# Revit family: FU_Chair_Sandler_Zenpro 0010
name_source: partatom
category: Furniture
units: mm (PartAtom-declared; Revit-internal decimal feet)

## family parameters
Always vertical = Yes
Cut with Voids When Loaded = No
OmniClass Number = 23.40.20.00
OmniClass Title = General Furniture and Specialties
Render Appearance Source = Family Geometry
Room Calculation Point = No
Shared = No
Work Plane-Based = No

## types (1)
- Zenpro 0010
    Default Elevation = 0 mm  [stored 0 ft]
    Depth = 640 mm  [stored 2.09974 ft]
    Description = A sophisticated executive armchair designed for comfortable sitting throughout the working day. Suitable for executive offices and boardrooms, it features a weight-activated, synchronized tilt mechanism that can be locked in seven positions and fine-tuned using the tension control knob. The aluminum arms are padded and there is a pneumatic seat adjustment mechanism.

Soft-tread caster wheels and aluminum frame. Designed by Mario Ruiz. Greenguard Gold-certified to minimize the impact on indoor air quality. A sustainable chair that is 99% recyclable and made of 43% recycled materials.
    Height = 1277 mm
    Manufacturer = Sandler
    Model = Zenpro 0120
    URL = https://www.sandlerseating.com
    Width = 680 mm  [stored 2.23097 ft]

note: [stored X ft] marks values corroborated as IEEE doubles in the binary element streams (Revit-internal decimal feet)

## geometry (parser evidence)
native form markers: Sweep x9
no freeform markers — native parametric forms only
